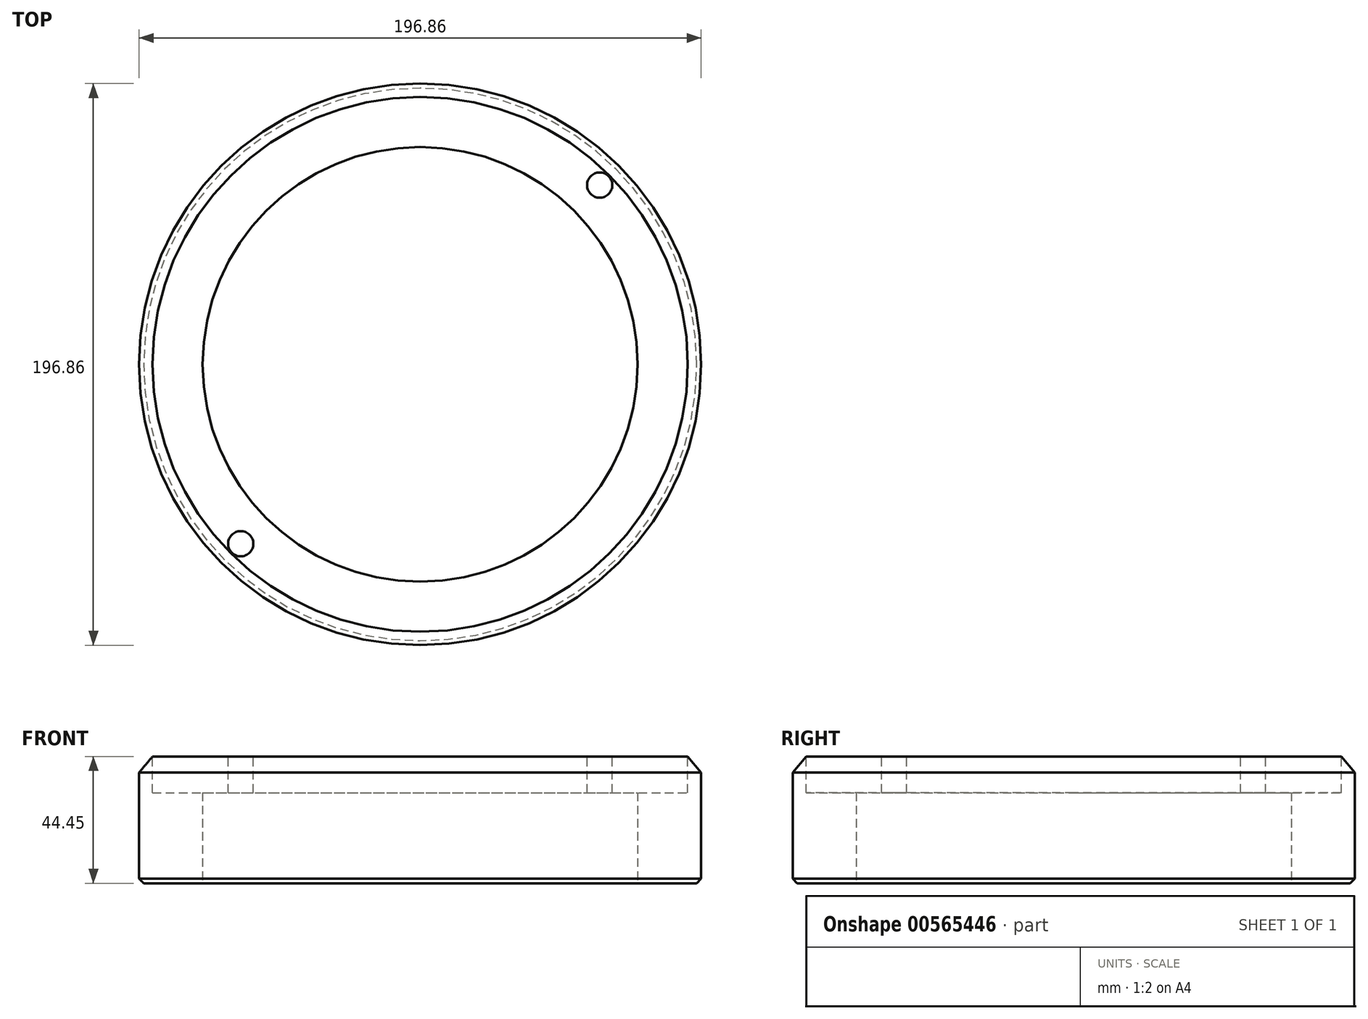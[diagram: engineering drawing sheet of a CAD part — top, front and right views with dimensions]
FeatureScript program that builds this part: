
annotation { "Feature Type Name" : "Feature", "Feature Type Description" : "" }
export const myFeature = defineFeature(function(context is Context, id is Id, definition is map)
    precondition{}
    {
        {
            var Q0;
            Q0=qCreatedBy(makeId("Front.planeOp"),FACE);
            var sketch = newSketch(context, id + "F0", { "sketchPlane" : qUnion([Q0])});
            skLineSegment(sketch, "E0", {"start": v(0, 0) * mm, "end": v(98.43, 0) * mm});
            skLineSegment(sketch, "E1", {"start": v(98.43, 0) * mm, "end": v(98.43, -38.85) * mm});
            skLineSegment(sketch, "E2", {"start": v(98.43, -38.85) * mm, "end": v(93.73, -44.45) * mm});
            skLineSegment(sketch, "E3", {"start": v(93.73, -44.45) * mm, "end": v(0, -44.45) * mm});
            skLineSegment(sketch, "E4", {"start": v(0, -44.45) * mm, "end": v(0, 0) * mm});
            skSolve(sketch);
        }
        {
            var Q0;
            Q0=qSketchRegion(id+"F0",true);
            var Q1;
            Q1=sQuery(id+"F0.wireOp",EDGE,"E4");
            revolve(context, id + "F1", {"entities" : qUnion([Q0]), "axis" : qUnion([Q1]), "revolveType" : RevolveType.FULL});
        }
        {
            var Q0;
            Q0=makeQuery(id+"F1.opRevolve","SWEPT_EDGE",EDGE,{"disambiguationData":[OSD([sQuery(id+"F0.wireOp",EDGE,"E0"),sQuery(id+"F0.wireOp",EDGE,"E1")])]});
            chamfer(context, id + "F2", {"entities" : qUnion([Q0]), "chamferType" : ChamferType.OFFSET_ANGLE, "width" : 1.57 * mm, "oppositeDirection" : false, "angle" : 45 * degree, "tangentPropagation" : true});
        }
        {
            var Q0;
            Q0=makeQuery(id+"F1.opRevolve","SWEPT_FACE",FACE,{"disambiguationData":[OSD([sQuery(id+"F0.wireOp",EDGE,"E3")])]});
            var sketch = newSketch(context, id + "F3", { "sketchPlane" : qUnion([Q0])});
            skLineSegment(sketch, "E5", {"start": v(-173.3, 0) * mm, "end": v(188.3, 0) * mm, "construction": true});
            skLineSegment(sketch, "E6", {"start": v(0, 128.5) * mm, "end": v(0, -161.91) * mm, "construction": true});
            skLineSegment(sketch, "E7", {"start": v(0, 0) * mm, "end": v(44.02, -164.29) * mm, "construction": true});
            skCircle(sketch, "E8", {"center": v(0, 0) * mm, "radius": 88.9 * mm});
            skCircle(sketch, "E9", {"center": v(23, -85.87) * mm, "radius": 4.42 * mm});
            skCircle(sketch, "E10.1.0", {"center": v(85.87, -23) * mm, "radius": 4.42 * mm});
            skCircle(sketch, "E10.2.0", {"center": v(62.86, 62.86) * mm, "radius": 4.42 * mm});
            skCircle(sketch, "E10.3.0", {"center": v(-23, 85.87) * mm, "radius": 4.42 * mm});
            skCircle(sketch, "E10.4.0", {"center": v(-85.87, 23) * mm, "radius": 4.42 * mm});
            skCircle(sketch, "E10.5.0", {"center": v(-62.86, -62.86) * mm, "radius": 4.42 * mm});
            skSolve(sketch);
        }
        {
            var Q0;
            {var subQ0=sQuery(id+"F3.wireOp",EDGE,"E10.3.0");var subQ1=sQuery(id+"F3.wireOp",EDGE,"E8");var subQ2=makeQuery(id+"F3.imprint","INTERSECT",VERTEX,{"disambiguationData":[OD(0.0)],"derivedFrom":[subQ1,subQ0]});Q0=makeQuery(id+"F3.imprint","IMPRINT",FACE,{"disambiguationData":[TD([[makeQuery(id+"F3.imprint","IMPRINT",EDGE,{"disambiguationData":[TD([[subQ2,-1.0]])],"derivedFrom":subQ1}),1.0]])]});}
            var Q1;
            {var subQ0=sQuery(id+"F3.wireOp",EDGE,"E10.3.0");var subQ1=sQuery(id+"F3.wireOp",EDGE,"E8");var subQ2=makeQuery(id+"F3.imprint","INTERSECT",VERTEX,{"disambiguationData":[OD(0.0)],"derivedFrom":[subQ1,subQ0]});Q1=makeQuery(id+"F3.imprint","IMPRINT",FACE,{"disambiguationData":[TD([[makeQuery(id+"F3.imprint","IMPRINT",EDGE,{"disambiguationData":[TD([[subQ2,-1.0]])],"derivedFrom":subQ1}),-1.0]])]});}
            var Q2;
            {var subQ0=sQuery(id+"F3.wireOp",EDGE,"E10.2.0");var subQ1=sQuery(id+"F3.wireOp",EDGE,"E8");var subQ2=makeQuery(id+"F3.imprint","INTERSECT",VERTEX,{"disambiguationData":[OD(0.0)],"derivedFrom":[subQ1,subQ0]});Q2=makeQuery(id+"F3.imprint","IMPRINT",FACE,{"disambiguationData":[TD([[makeQuery(id+"F3.imprint","IMPRINT",EDGE,{"disambiguationData":[TD([[subQ2,1.0]])],"derivedFrom":subQ1}),-1.0]])]});}
            var Q3;
            {var subQ0=sQuery(id+"F3.wireOp",EDGE,"E10.2.0");var subQ1=sQuery(id+"F3.wireOp",EDGE,"E8");var subQ2=makeQuery(id+"F3.imprint","INTERSECT",VERTEX,{"disambiguationData":[OD(0.0)],"derivedFrom":[subQ1,subQ0]});Q3=makeQuery(id+"F3.imprint","IMPRINT",FACE,{"disambiguationData":[TD([[makeQuery(id+"F3.imprint","IMPRINT",EDGE,{"disambiguationData":[TD([[subQ2,1.0]])],"derivedFrom":subQ1}),1.0]])]});}
            var Q4;
            {var subQ0=sQuery(id+"F3.wireOp",EDGE,"E10.4.0");var subQ1=sQuery(id+"F3.wireOp",EDGE,"E8");var subQ2=makeQuery(id+"F3.imprint","INTERSECT",VERTEX,{"disambiguationData":[OD(0.0)],"derivedFrom":[subQ1,subQ0]});Q4=makeQuery(id+"F3.imprint","IMPRINT",FACE,{"disambiguationData":[TD([[makeQuery(id+"F3.imprint","IMPRINT",EDGE,{"disambiguationData":[TD([[subQ2,-1.0]])],"derivedFrom":subQ1}),-1.0]])]});}
            var Q5;
            {var subQ0=sQuery(id+"F3.wireOp",EDGE,"E10.4.0");var subQ1=sQuery(id+"F3.wireOp",EDGE,"E8");var subQ2=makeQuery(id+"F3.imprint","INTERSECT",VERTEX,{"disambiguationData":[OD(0.0)],"derivedFrom":[subQ1,subQ0]});Q5=makeQuery(id+"F3.imprint","IMPRINT",FACE,{"disambiguationData":[TD([[makeQuery(id+"F3.imprint","IMPRINT",EDGE,{"disambiguationData":[TD([[subQ2,-1.0]])],"derivedFrom":subQ1}),1.0]])]});}
            var Q6;
            {var subQ0=sQuery(id+"F3.wireOp",EDGE,"E10.5.0");var subQ1=sQuery(id+"F3.wireOp",EDGE,"E8");var subQ2=makeQuery(id+"F3.imprint","INTERSECT",VERTEX,{"disambiguationData":[OD(0.0)],"derivedFrom":[subQ1,subQ0]});Q6=makeQuery(id+"F3.imprint","IMPRINT",FACE,{"disambiguationData":[TD([[makeQuery(id+"F3.imprint","IMPRINT",EDGE,{"disambiguationData":[TD([[subQ2,-1.0]])],"derivedFrom":subQ1}),1.0]])]});}
            var Q7;
            {var subQ0=sQuery(id+"F3.wireOp",EDGE,"E10.5.0");var subQ1=sQuery(id+"F3.wireOp",EDGE,"E8");var subQ2=makeQuery(id+"F3.imprint","INTERSECT",VERTEX,{"disambiguationData":[OD(0.0)],"derivedFrom":[subQ1,subQ0]});Q7=makeQuery(id+"F3.imprint","IMPRINT",FACE,{"disambiguationData":[TD([[makeQuery(id+"F3.imprint","IMPRINT",EDGE,{"disambiguationData":[TD([[subQ2,-1.0]])],"derivedFrom":subQ1}),-1.0]])]});}
            var Q8;
            {var subQ0=sQuery(id+"F3.wireOp",EDGE,"E9");var subQ1=sQuery(id+"F3.wireOp",EDGE,"E8");var subQ2=makeQuery(id+"F3.imprint","INTERSECT",VERTEX,{"disambiguationData":[OD(0.0)],"derivedFrom":[subQ1,subQ0]});Q8=makeQuery(id+"F3.imprint","IMPRINT",FACE,{"disambiguationData":[TD([[makeQuery(id+"F3.imprint","IMPRINT",EDGE,{"disambiguationData":[TD([[subQ2,-1.0]])],"derivedFrom":subQ1}),1.0]])]});}
            var Q9;
            {var subQ0=sQuery(id+"F3.wireOp",EDGE,"E9");var subQ1=sQuery(id+"F3.wireOp",EDGE,"E8");var subQ2=makeQuery(id+"F3.imprint","INTERSECT",VERTEX,{"disambiguationData":[OD(0.0)],"derivedFrom":[subQ1,subQ0]});Q9=makeQuery(id+"F3.imprint","IMPRINT",FACE,{"disambiguationData":[TD([[makeQuery(id+"F3.imprint","IMPRINT",EDGE,{"disambiguationData":[TD([[subQ2,-1.0]])],"derivedFrom":subQ1}),-1.0]])]});}
            var Q10;
            {var subQ0=sQuery(id+"F3.wireOp",EDGE,"E10.1.0");var subQ1=sQuery(id+"F3.wireOp",EDGE,"E8");var subQ2=makeQuery(id+"F3.imprint","INTERSECT",VERTEX,{"disambiguationData":[OD(0.0)],"derivedFrom":[subQ1,subQ0]});Q10=makeQuery(id+"F3.imprint","IMPRINT",FACE,{"disambiguationData":[TD([[makeQuery(id+"F3.imprint","IMPRINT",EDGE,{"disambiguationData":[TD([[subQ2,-1.0]])],"derivedFrom":subQ1}),1.0]])]});}
            var Q11;
            {var subQ0=sQuery(id+"F3.wireOp",EDGE,"E10.1.0");var subQ1=sQuery(id+"F3.wireOp",EDGE,"E8");var subQ2=makeQuery(id+"F3.imprint","INTERSECT",VERTEX,{"disambiguationData":[OD(0.0)],"derivedFrom":[subQ1,subQ0]});Q11=makeQuery(id+"F3.imprint","IMPRINT",FACE,{"disambiguationData":[TD([[makeQuery(id+"F3.imprint","IMPRINT",EDGE,{"disambiguationData":[TD([[subQ2,-1.0]])],"derivedFrom":subQ1}),-1.0]])]});}
            var Q12;
            Q12=sQuery(id+"F3.wireOp",EDGE,"E10.3.0");
            var Q13;
            Q13=sQuery(id+"F3.wireOp",EDGE,"E10.4.0");
            var Q14;
            Q14=sQuery(id+"F3.wireOp",EDGE,"E10.2.0");
            var Q15;
            Q15=sQuery(id+"F3.wireOp",EDGE,"E10.1.0");
            var Q16;
            Q16=sQuery(id+"F3.wireOp",EDGE,"E9");
            var Q17;
            Q17=sQuery(id+"F3.wireOp",EDGE,"E10.5.0");
            extrude(context, id + "F4", {"entities" : qUnion([Q0, Q1, Q2, Q3, Q4, Q5, Q6, Q7, Q8, Q9, Q10, Q11]), "operationType" : NewBodyOperationType.REMOVE, "surfaceEntities" : qUnion([Q12, Q13, Q14, Q15, Q16, Q17]), "oppositeDirection" : true, "depth" : 12.7 * mm, "offsetDistance" : 25.4 * mm});
        }
        {
            var Q0;
            Q0=makeQuery(id+"F1.opRevolve","SWEPT_FACE",FACE,{"disambiguationData":[OSD([sQuery(id+"F0.wireOp",EDGE,"E0")])]});
            var sketch = newSketch(context, id + "F5", { "sketchPlane" : qUnion([Q0])});
            skCircle(sketch, "E11", {"center": v(0, 0) * mm, "radius": 76.2 * mm});
            skSolve(sketch);
        }
        {
            var Q0;
            Q0=qSketchRegion(id+"F5",true);
            extrude(context, id + "F6", {"entities" : qUnion([Q0]), "operationType" : NewBodyOperationType.REMOVE, "endBound" : BoundingType.THROUGH_ALL, "oppositeDirection" : true, "depth" : 25.4 * mm, "offsetDistance" : 25.4 * mm});
        }
        {
            var Q0;
            Q0=qCreatedBy(makeId("Front.planeOp"),FACE);
            var sketch = newSketch(context, id + "F7", { "sketchPlane" : qUnion([Q0])});
            skLineSegment(sketch, "E12", {"start": v(111.49, 0) * mm, "end": v(-102.87, 0) * mm, "construction": true});
            skSolve(sketch);
        }
        {
            var Q0;
            Q0=makeQuery(id+"F1.opRevolve","SWEPT_BODY",BODY,{"disambiguationData":[OSD([sQuery(id+"F0.wireOp",EDGE,"E0"),sQuery(id+"F0.wireOp",EDGE,"E1"),sQuery(id+"F0.wireOp",EDGE,"E2"),sQuery(id+"F0.wireOp",EDGE,"E3"),sQuery(id+"F0.wireOp",EDGE,"E4")])]});
            var Q1;
            Q1=sQuery(id+"F7.wireOp",EDGE,"E12");
            transform(context, id + "F8", {"entities" : qUnion([Q0]), "transformType" : TransformType.ROTATION, "transformAxis" : qUnion([Q1]), "angle" : 180 * degree, "makeCopy" : false});
        }
        {
            var Q0;
            Q0=makeQuery(id+"F1.opRevolve","SWEPT_BODY",BODY,{"disambiguationData":[OSD([sQuery(id+"F0.wireOp",EDGE,"E0"),sQuery(id+"F0.wireOp",EDGE,"E1"),sQuery(id+"F0.wireOp",EDGE,"E2"),sQuery(id+"F0.wireOp",EDGE,"E3"),sQuery(id+"F0.wireOp",EDGE,"E4")])]});
            transform(context, id + "F9", {"entities" : qUnion([Q0]), "transformType" : TransformType.TRANSLATION_3D, "dx" : 0 * mm, "dy" : 0 * mm, "dz" : -44.45 * mm, "makeCopy" : false});
        }
    });
